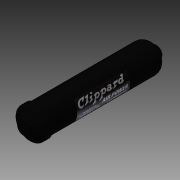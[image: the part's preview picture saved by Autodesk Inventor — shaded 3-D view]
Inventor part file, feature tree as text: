
AUTODESK INVENTOR PART (.ipt)
format: ipt  version: 2018 (Build 220112000, 112)  size: 185,856 bytes
history: native  units: in
note: dims shown in document units (in); Inventor stores cm internally (conversion verified against a paired STEP export)
features: sketch x8, extrude x4, revolve x3, fillet x2, other x2, projected_geometry x2, plane x1
ambient origin geometry x8: Origin, YZ Plane, XZ Plane, XY Plane, X Axis, Y Axis, Z Axis, Center Point
bodies: Solid1 (feature_tree)
feature tree (22):
  revolve  "Revolution1"  [1 undecoded]
  fillet  "Fillet1"  [1 undecoded]
  revolve  "Revolution2"  [1 undecoded]
  fillet  "Fillet2"  Radius=0.75in
  revolve  "Revolution3"  [1 undecoded]
  extrude  "Extrusion1"  Depth=0.144in TaperAngle=0.0deg
  extrude  "Extrusion2"  Depth=0.1in TaperAngle=0.0deg
  extrude  "Extrusion3"  [1 undecoded]
  extrude  "Extrusion4"  [1 undecoded]
  plane  "Work Plane1"
  other  "Decal1"
  sketch  "Sketch1"  dims[d0=1.28in d1=10.459in d2=90.0deg]
  sketch  "Sketch2"  dims[d3=0.75in d4=1.39in d5=0.75in]
  sketch  "Sketch3"  dims[d6=90.0deg d7=0.25in]
  sketch  "Sketch4"  dims[d8=90.0deg d9=0.144in d10=0.0in]
  projected_geometry  "Projected Loop1"
  sketch  "Sketch5"  dims[d11=0.322in d12=0.0in d13=0.1in d14=0.0in]
  projected_geometry  "Projected Loop2"
  sketch  "Sketch6"  dims[d15=0.1in d16=0.0in]
  sketch  "Sketch7"
  sketch  "Sketch8"
  other  "Image1"
note: 6 required parameter values undecoded (feature->parameter linkage not recoverable at this tier; creation-order binding heuristic only, values carry confidence <= 0.55)